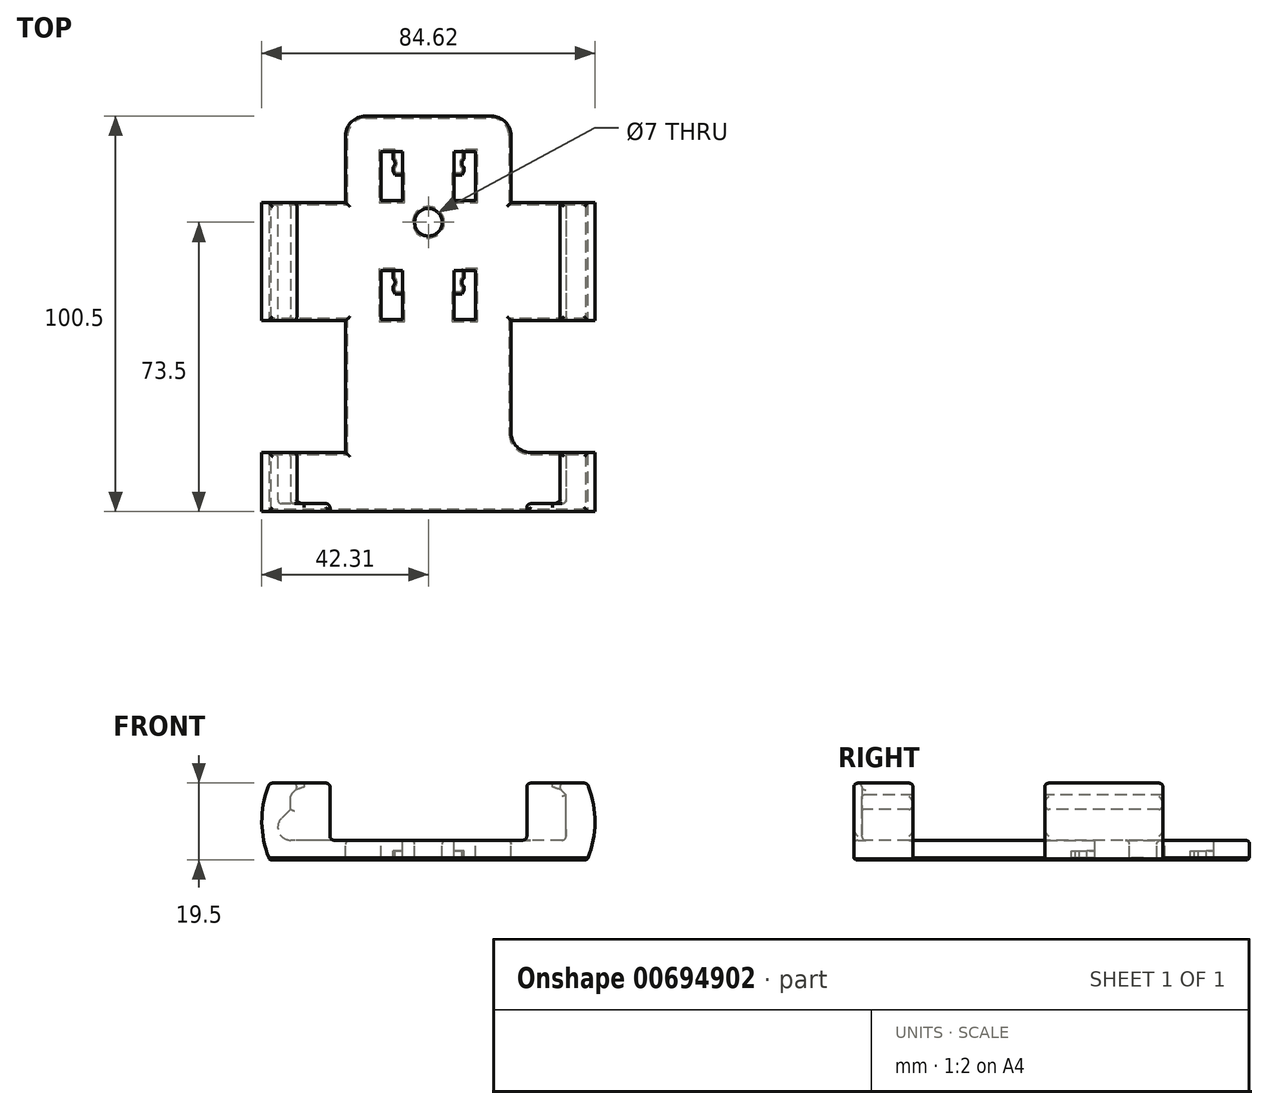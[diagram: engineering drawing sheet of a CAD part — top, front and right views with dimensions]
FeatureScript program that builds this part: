
annotation { "Feature Type Name" : "Feature", "Feature Type Description" : "" }
export const myFeature = defineFeature(function(context is Context, id is Id, definition is map)
    precondition{}
    {
        {
            var Q0;
            Q0=qCreatedBy(makeId("Top.planeOp"),FACE);
            var sketch = newSketch(context, id + "F0", { "sketchPlane" : qUnion([Q0])});
            skLineSegment(sketch, "E0.bottom", {"start": v(-35, 71.5) * mm, "end": v(35, 71.5) * mm});
            skLineSegment(sketch, "E0.top", {"start": v(-35, -71.5) * mm, "end": v(35, -71.5) * mm});
            skLineSegment(sketch, "E0.left", {"start": v(-35, 71.5) * mm, "end": v(-35, -71.5) * mm});
            skLineSegment(sketch, "E0.right", {"start": v(35, 71.5) * mm, "end": v(35, -71.5) * mm});
            skLineSegment(sketch, "E1", {"start": v(35, 71.5) * mm, "end": v(0, 0) * mm, "construction": true});
            skLineSegment(sketch, "E2.bottom", {"start": v(-55, 35.5) * mm, "end": v(55, 35.5) * mm});
            skLineSegment(sketch, "E2.top", {"start": v(-55, 16.5) * mm, "end": v(55, 16.5) * mm});
            skLineSegment(sketch, "E2.left", {"start": v(-55, 35.5) * mm, "end": v(-55, 16.5) * mm});
            skLineSegment(sketch, "E2.right", {"start": v(55, 35.5) * mm, "end": v(55, 16.5) * mm});
            skLineSegment(sketch, "E3.bottom", {"start": v(-35, 71.5) * mm, "end": v(-38.25, 71.5) * mm});
            skLineSegment(sketch, "E3.top", {"start": v(-35, -71.5) * mm, "end": v(-38.25, -71.5) * mm});
            skLineSegment(sketch, "E3.right", {"start": v(-38.25, 71.5) * mm, "end": v(-38.25, -71.5) * mm});
            skLineSegment(sketch, "E4", {"start": v(-35, 71.5) * mm, "end": v(0, 0) * mm, "construction": true});
            skLineSegment(sketch, "E5", {"start": v(0, 0) * mm, "end": v(-35, -71.5) * mm, "construction": true});
            skLineSegment(sketch, "E6", {"start": v(0, 0) * mm, "end": v(35, -71.5) * mm, "construction": true});
            skSolve(sketch);
        }
        {
            var Q0;
            Q0=qCreatedBy(makeId("Top.planeOp"),FACE);
            var sketch = newSketch(context, id + "F1", { "sketchPlane" : qUnion([Q0])});
            skLineSegment(sketch, "E7", {"start": v(-12, 5.5) * mm, "end": v(-6.5, 5.5) * mm});
            skLineSegment(sketch, "E8", {"start": v(-6.5, 5.5) * mm, "end": v(-6.5, 12) * mm});
            skLineSegment(sketch, "E9", {"start": v(-6.5, 12) * mm, "end": v(-8.5, 12) * mm});
            skLineSegment(sketch, "E10", {"start": v(-8.5, 12) * mm, "end": v(-9, 13) * mm});
            skLineSegment(sketch, "E11", {"start": v(-9, 13) * mm, "end": v(-9, 14) * mm});
            skLineSegment(sketch, "E12", {"start": v(-12, 5.5) * mm, "end": v(-12, 18) * mm});
            skLineSegment(sketch, "E13", {"start": v(-12, 18) * mm, "end": v(-9, 18) * mm});
            skLineSegment(sketch, "E14", {"start": v(-9, 18) * mm, "end": v(-9, 16) * mm});
            skLineSegment(sketch, "E15", {"start": v(-9, 16) * mm, "end": v(-9, 14) * mm, "construction": true});
            skLineSegment(sketch, "E16", {"start": v(-9, 15) * mm, "end": v(-8.5, 15) * mm, "construction": true});
            skArc(sketch, "E17", {"start": v(-9, 14) * mm, "mid": v(-8.5, 15) * mm, "end": v(-9, 16) * mm});
            skLineSegment(sketch, "E18", {"start": v(-9, 18) * mm, "end": v(-6.5, 18) * mm});
            skLineSegment(sketch, "E19", {"start": v(-6.5, 12) * mm, "end": v(-6.5, 18) * mm});
            skLineSegment(sketch, "E20", {"start": v(-12, -24.75) * mm, "end": v(-6.5, -24.75) * mm});
            skLineSegment(sketch, "E21", {"start": v(-6.5, -24.75) * mm, "end": v(-6.5, -18.25) * mm});
            skLineSegment(sketch, "E22", {"start": v(-6.5, -18.25) * mm, "end": v(-8.5, -18.25) * mm});
            skLineSegment(sketch, "E23", {"start": v(-8.5, -18.25) * mm, "end": v(-9, -17.25) * mm});
            skLineSegment(sketch, "E24", {"start": v(-9, -17.25) * mm, "end": v(-9, -16.25) * mm});
            skLineSegment(sketch, "E25", {"start": v(-12, -24.75) * mm, "end": v(-12, -12.25) * mm});
            skLineSegment(sketch, "E26", {"start": v(-12, -12.25) * mm, "end": v(-9, -12.25) * mm});
            skLineSegment(sketch, "E27", {"start": v(-9, -12.25) * mm, "end": v(-9, -14.25) * mm});
            skLineSegment(sketch, "E28", {"start": v(-9, -14.25) * mm, "end": v(-9, -16.25) * mm, "construction": true});
            skLineSegment(sketch, "E29", {"start": v(-9, -15.25) * mm, "end": v(-8.5, -15.25) * mm, "construction": true});
            skArc(sketch, "E30", {"start": v(-9, -16.25) * mm, "mid": v(-8.5, -15.25) * mm, "end": v(-9, -14.25) * mm});
            skLineSegment(sketch, "E31", {"start": v(-9, -12.25) * mm, "end": v(-6.5, -12.25) * mm});
            skLineSegment(sketch, "E32", {"start": v(-6.5, -18.25) * mm, "end": v(-6.5, -12.25) * mm});
            skLineSegment(sketch, "E33", {"start": v(-12, 18) * mm, "end": v(-15.54, 21.53) * mm, "construction": true});
            skLineSegment(sketch, "E34", {"start": v(-6.5, 18) * mm, "end": v(-7.92, 19.4) * mm, "construction": true});
            skLineSegment(sketch, "E35.MirrorCS", {"start": v(9, 15) * mm, "end": v(8.5, 15) * mm, "construction": true});
            skLineSegment(sketch, "E36.MirrorCS", {"start": v(9, 16) * mm, "end": v(9, 14) * mm, "construction": true});
            skLineSegment(sketch, "E37.MirrorCS", {"start": v(9, -14.25) * mm, "end": v(9, -16.25) * mm, "construction": true});
            skLineSegment(sketch, "E38.MirrorCS", {"start": v(9, 18) * mm, "end": v(9, 16) * mm});
            skArc(sketch, "E39.MirrorCS", {"start": v(9, 14) * mm, "mid": v(8.5, 15) * mm, "end": v(9, 16) * mm});
            skLineSegment(sketch, "E40.MirrorCS", {"start": v(8.5, -18.25) * mm, "end": v(9, -17.25) * mm});
            skArc(sketch, "E41.MirrorCS", {"start": v(9, -16.25) * mm, "mid": v(8.5, -15.25) * mm, "end": v(9, -14.25) * mm});
            skLineSegment(sketch, "E42.MirrorCS", {"start": v(8.5, 12) * mm, "end": v(9, 13) * mm});
            skLineSegment(sketch, "E43.MirrorCS", {"start": v(9, 13) * mm, "end": v(9, 14) * mm});
            skLineSegment(sketch, "E44.MirrorCS", {"start": v(9, -17.25) * mm, "end": v(9, -16.25) * mm});
            skLineSegment(sketch, "E45.MirrorCS", {"start": v(9, -15.25) * mm, "end": v(8.5, -15.25) * mm, "construction": true});
            skLineSegment(sketch, "E46.MirrorCS", {"start": v(9, -12.25) * mm, "end": v(9, -14.25) * mm});
            skLineSegment(sketch, "E47.MirrorCS", {"start": v(12, 18) * mm, "end": v(15.54, 21.53) * mm, "construction": true});
            skLineSegment(sketch, "E48.MirrorCS", {"start": v(6.5, 18) * mm, "end": v(7.92, 19.4) * mm, "construction": true});
            skLineSegment(sketch, "E49.MirrorCS", {"start": v(6.5, -18.25) * mm, "end": v(8.5, -18.25) * mm});
            skLineSegment(sketch, "E50.MirrorCS", {"start": v(6.5, 12) * mm, "end": v(8.5, 12) * mm});
            skLineSegment(sketch, "E51.MirrorCS", {"start": v(9, -12.25) * mm, "end": v(6.5, -12.25) * mm});
            skLineSegment(sketch, "E52.MirrorCS", {"start": v(12, 18) * mm, "end": v(9, 18) * mm});
            skLineSegment(sketch, "E53.MirrorCS", {"start": v(9, 18) * mm, "end": v(6.5, 18) * mm});
            skLineSegment(sketch, "E54.MirrorCS", {"start": v(12, -12.25) * mm, "end": v(9, -12.25) * mm});
            skLineSegment(sketch, "E55.MirrorCS", {"start": v(6.5, -18.25) * mm, "end": v(6.5, -12.25) * mm});
            skLineSegment(sketch, "E56.MirrorCS", {"start": v(6.5, 12) * mm, "end": v(6.5, 18) * mm});
            skLineSegment(sketch, "E57.MirrorCS", {"start": v(6.5, -24.75) * mm, "end": v(6.5, -18.25) * mm});
            skLineSegment(sketch, "E58.MirrorCS", {"start": v(12, 5.5) * mm, "end": v(6.5, 5.5) * mm});
            skLineSegment(sketch, "E59.MirrorCS", {"start": v(6.5, 5.5) * mm, "end": v(6.5, 12) * mm});
            skLineSegment(sketch, "E60.MirrorCS", {"start": v(12, -24.75) * mm, "end": v(6.5, -24.75) * mm});
            skLineSegment(sketch, "E61.MirrorCS", {"start": v(12, 5.5) * mm, "end": v(12, 18) * mm});
            skLineSegment(sketch, "E62.MirrorCS", {"start": v(12, -24.75) * mm, "end": v(12, -12.25) * mm});
            skSolve(sketch);
        }
        {
            var Q0;
            Q0=qCreatedBy(makeId("Top.planeOp"),FACE);
            var sketch = newSketch(context, id + "F2", { "sketchPlane" : qUnion([Q0])});
            skLineSegment(sketch, "E63.bottom", {"start": v(-21, 27) * mm, "end": v(21, 27) * mm});
            skLineSegment(sketch, "E63.top", {"start": v(-21, -27) * mm, "end": v(21, -27) * mm});
            skLineSegment(sketch, "E63.left", {"start": v(-21, 27) * mm, "end": v(-21, -27) * mm});
            skLineSegment(sketch, "E63.right", {"start": v(21, 27) * mm, "end": v(21, -27) * mm});
            skLineSegment(sketch, "E64", {"start": v(21, 27) * mm, "end": v(-21, -27) * mm, "construction": true});
            skLineSegment(sketch, "E65.top", {"start": v(-21, -71.5) * mm, "end": v(21, -71.5) * mm});
            skLineSegment(sketch, "E65.left", {"start": v(-21, -27) * mm, "end": v(-21, -71.5) * mm});
            skLineSegment(sketch, "E65.right", {"start": v(21, -27) * mm, "end": v(21, -71.5) * mm});
            skLineSegment(sketch, "E66.bottom", {"start": v(-21, 5) * mm, "end": v(-40.25, 5) * mm});
            skLineSegment(sketch, "E66.top", {"start": v(-21, -25) * mm, "end": v(-40.25, -25) * mm});
            skLineSegment(sketch, "E66.left", {"start": v(-21, 5) * mm, "end": v(-21, -25) * mm});
            skLineSegment(sketch, "E66.right", {"start": v(-40.25, 5) * mm, "end": v(-40.25, -25) * mm});
            skLineSegment(sketch, "E67.bottom", {"start": v(21, 5) * mm, "end": v(40.25, 5) * mm});
            skLineSegment(sketch, "E67.top", {"start": v(21, -25) * mm, "end": v(40.25, -25) * mm});
            skLineSegment(sketch, "E67.left", {"start": v(21, 5) * mm, "end": v(21, -25) * mm});
            skLineSegment(sketch, "E67.right", {"start": v(40.25, 5) * mm, "end": v(40.25, -25) * mm});
            skLineSegment(sketch, "E68.bottom", {"start": v(-40.25, -58.5) * mm, "end": v(40.25, -58.5) * mm});
            skLineSegment(sketch, "E68.top", {"start": v(-40.25, -73.5) * mm, "end": v(40.25, -73.5) * mm});
            skLineSegment(sketch, "E68.left", {"start": v(-40.25, -58.5) * mm, "end": v(-40.25, -73.5) * mm});
            skLineSegment(sketch, "E68.right", {"start": v(40.25, -58.5) * mm, "end": v(40.25, -73.5) * mm});
            skPoint(sketch, "E69", {"position": v(0, 20) * mm});
            skPoint(sketch, "E70", {"position": v(0, -20) * mm});
            skSolve(sketch);
        }
        {
            var Q0;
            Q0=qCreatedBy(makeId("Front.planeOp"),FACE);
            var Q1;
            Q1=sQuery(id+"F2.wireOp",VERTEX,"E65.top.start");
            cPlane(context, id + "F3", {"entities" : qUnion([Q0, Q1]), "cplaneType" : CPlaneType.PLANE_POINT, "offset" : 25 * mm, "width" : 150 * mm, "height" : 150 * mm});
        }
        {
            var Q0;
            Q0=qCreatedBy(id+"F3.planeOp",FACE);
            var sketch = newSketch(context, id + "F4", { "sketchPlane" : qUnion([Q0])});
            skLineSegment(sketch, "E71", {"start": v(35, 0) * mm, "end": v(-35, 0) * mm});
            skLineSegment(sketch, "E72", {"start": v(-32, 14.5) * mm, "end": v(-40.31, 14.5) * mm});
            skLineSegment(sketch, "E73", {"start": v(-40.31, -5) * mm, "end": v(40.31, -5) * mm});
            skLineSegment(sketch, "E74", {"start": v(40.31, 14.5) * mm, "end": v(32, 14.5) * mm});
            skLineSegment(sketch, "E75", {"start": v(32, 14.5) * mm, "end": v(32, 14.5) * mm});
            skArc(sketch, "E76", {"start": v(-40.31, 14.5) * mm, "mid": v(-42.31, 4.75) * mm, "end": v(-40.31, -5) * mm});
            skArc(sketch, "E77", {"start": v(40.31, -5) * mm, "mid": v(42.31, 4.75) * mm, "end": v(40.31, 14.5) * mm});
            skLineSegment(sketch, "E78", {"start": v(-32, 14.5) * mm, "end": v(-25, 14.5) * mm});
            skLineSegment(sketch, "E79", {"start": v(-25, 14.5) * mm, "end": v(-25, 0) * mm});
            skLineSegment(sketch, "E80", {"start": v(32, 14.5) * mm, "end": v(25, 14.5) * mm});
            skLineSegment(sketch, "E81", {"start": v(25, 14.5) * mm, "end": v(25, 0) * mm});
            skLineSegment(sketch, "E82", {"start": v(-32, 14.5) * mm, "end": v(-33.5, 13) * mm});
            skLineSegment(sketch, "E83", {"start": v(-33.5, 13) * mm, "end": v(-35, 11.5) * mm});
            skLineSegment(sketch, "E84", {"start": v(35, 0) * mm, "end": v(35, 6.5) * mm});
            skLineSegment(sketch, "E85", {"start": v(35, 6.5) * mm, "end": v(35, 11.5) * mm});
            skLineSegment(sketch, "E86", {"start": v(32, 14.5) * mm, "end": v(35, 11.5) * mm});
            skLineSegment(sketch, "E87", {"start": v(-40.31, 14.5) * mm, "end": v(-40.31, -5) * mm, "construction": true});
            skArc(sketch, "E88", {"start": v(-35, 0) * mm, "mid": v(-38, 2) * mm, "end": v(-37.3, 5.55) * mm});
            skLineSegment(sketch, "E89", {"start": v(-35, 7.85) * mm, "end": v(-37.3, 5.55) * mm});
            skLineSegment(sketch, "E90", {"start": v(-35, 7.85) * mm, "end": v(-35, 11.5) * mm});
            skLineSegment(sketch, "E91", {"start": v(-37.3, 5.55) * mm, "end": v(-37.3, 5.55) * mm});
            skArc(sketch, "E92", {"start": v(-37.3, 5.55) * mm, "mid": v(-36.24, 6.25) * mm, "end": v(-35, 6.5) * mm, "construction": true});
            skPoint(sketch, "E93.orphan", {"position": v(-49.26, 0) * mm});
            skSolve(sketch);
        }
        {
            var Q0;
            Q0=makeQuery(id+"F4.imprint","IMPRINT",FACE,{"disambiguationData":[TD([[makeQuery(id+"F4.imprint","IMPRINT",EDGE,{"derivedFrom":sQuery(id+"F4.wireOp",EDGE,"E72")}),1.0]])]});
            var Q1;
            Q1=sQuery(id+"F2.wireOp",VERTEX,"E68.bottom.start");
            extrude(context, id + "F5", {"entities" : qUnion([Q0]), "endBound" : BoundingType.UP_TO_VERTEX, "oppositeDirection" : true, "depth" : 25 * mm, "endBoundEntityVertex" : qUnion([Q1]), "offsetDistance" : 25 * mm});
        }
        {
            var Q0;
            Q0=makeQuery(id+"F4.imprint","IMPRINT",FACE,{"disambiguationData":[TD([[makeQuery(id+"F4.imprint","IMPRINT",EDGE,{"derivedFrom":sQuery(id+"F4.wireOp",EDGE,"E78")}),-1.0]])]});
            var Q1;
            Q1=makeQuery(id+"F4.imprint","IMPRINT",FACE,{"disambiguationData":[TD([[makeQuery(id+"F4.imprint","IMPRINT",EDGE,{"derivedFrom":sQuery(id+"F4.wireOp",EDGE,"E80")}),1.0]])]});
            var Q2;
            Q2=makeQuery(id+"F4.imprint","IMPRINT",FACE,{"disambiguationData":[TD([[makeQuery(id+"F4.imprint","IMPRINT",EDGE,{"derivedFrom":sQuery(id+"F4.wireOp",EDGE,"E72")}),1.0]])]});
            var Q3;
            Q3=sQuery(id+"F2.wireOp",VERTEX,"E68.left.end");
            extrude(context, id + "F6", {"entities" : qUnion([Q0, Q1, Q2]), "operationType" : NewBodyOperationType.ADD, "endBound" : BoundingType.UP_TO_VERTEX, "depth" : 25 * mm, "endBoundEntityVertex" : qUnion([Q3]), "offsetDistance" : 25 * mm});
        }
        {
            var Q0;
            Q0=makeQuery(id+"F4.imprint","IMPRINT",FACE,{"disambiguationData":[TD([[makeQuery(id+"F4.imprint","IMPRINT",EDGE,{"derivedFrom":sQuery(id+"F4.wireOp",EDGE,"E72")}),1.0]])]});
            var Q1;
            Q1=sQuery(id+"F2.wireOp",VERTEX,"E67.bottom.end");
            var Q2;
            Q2=sQuery(id+"F2.wireOp",VERTEX,"E67.right.end");
            extrude(context, id + "F7", {"entities" : qUnion([Q0]), "endBound" : BoundingType.UP_TO_VERTEX, "oppositeDirection" : true, "depth" : 25 * mm, "endBoundEntityVertex" : qUnion([Q1]), "offsetDistance" : 25 * mm, "hasSecondDirection" : true, "secondDirectionBound" : SecondDirectionBoundingType.UP_TO_VERTEX, "secondDirectionOppositeDirection" : true, "secondDirectionDepth" : 25 * mm, "secondDirectionBoundEntityVertex" : qUnion([Q2])});
        }
        {
            var Q0;
            {var subQ1=sQuery(id+"F2.wireOp",EDGE,"E63.bottom");Q0=makeQuery(id+"F2.imprint","IMPRINT",FACE,{"disambiguationData":[TD([[makeQuery(id+"F2.imprint","IMPRINT",EDGE,{"derivedFrom":subQ1}),-1.0]])]});}
            var Q1;
            {var subQ0=sQuery(id+"F2.wireOp",EDGE,"E63.top");Q1=makeQuery(id+"F2.imprint","IMPRINT",FACE,{"disambiguationData":[TD([[makeQuery(id+"F2.imprint","IMPRINT",EDGE,{"derivedFrom":subQ0}),-1.0]])]});}
            var Q2;
            Q2=makeQuery(id+"F6.opExtrude","CAP_VERTEX",VERTEX,{"disambiguationData":[OSD([sQuery(id+"F4.wireOp",EDGE,"E73"),sQuery(id+"F4.wireOp",EDGE,"E76"),dummyQuery(id+"F6.vertexPlane.planeOp",FACE)])],"isStart":false});
            extrude(context, id + "F8", {"entities" : qUnion([Q0, Q1]), "endBound" : BoundingType.UP_TO_VERTEX, "oppositeDirection" : true, "depth" : 25 * mm, "endBoundEntityVertex" : qUnion([Q2]), "offsetDistance" : 25 * mm});
        }
        {
            var Q0;
            Q0=makeQuery(id+"F5.opExtrude","SWEPT_BODY",BODY,{"disambiguationData":[OSD([sQuery(id+"F4.wireOp",EDGE,"E71"),sQuery(id+"F4.wireOp",EDGE,"sbdDi5I9-Yebq-qmN7-GLHp-3G1XwB9cKRCZ"),sQuery(id+"F4.wireOp",EDGE,"7URjV5Ms-kFcT-YtzM-ZppO-VChNSRZk8awo"),sQuery(id+"F4.wireOp",EDGE,"zq0j43Qj-IFnj-aGb7-oLl1-zX5iOFrslPZI"),sQuery(id+"F4.wireOp",EDGE,"k48rp8DH-MXxx-a3kQ-F4OR-XtvpYe2jZDF6"),sQuery(id+"F4.wireOp",EDGE,"ZQmb1dzz-Gxe3-Qxpy-tlJK-SNzGoLeYOMF0"),sQuery(id+"F4.wireOp",EDGE,"E72"),sQuery(id+"F4.wireOp",EDGE,"E73"),sQuery(id+"F4.wireOp",EDGE,"E74"),sQuery(id+"F4.wireOp",EDGE,"E75"),sQuery(id+"F4.wireOp",EDGE,"qAfCrrqd-AJ75-G8RO-JwNo-VFnenWKlcyLA"),sQuery(id+"F4.wireOp",EDGE,"rlMWnyCU-j4gb-ryVS-FNKK-qwGZLt9JwQKd"),sQuery(id+"F4.wireOp",EDGE,"E76"),sQuery(id+"F4.wireOp",EDGE,"E77")])]});
            var Q1;
            Q1=makeQuery(id+"F7.opExtrude","SWEPT_BODY",BODY,{"disambiguationData":[OSD([sQuery(id+"F4.wireOp",EDGE,"E71"),sQuery(id+"F4.wireOp",EDGE,"sbdDi5I9-Yebq-qmN7-GLHp-3G1XwB9cKRCZ"),sQuery(id+"F4.wireOp",EDGE,"7URjV5Ms-kFcT-YtzM-ZppO-VChNSRZk8awo"),sQuery(id+"F4.wireOp",EDGE,"zq0j43Qj-IFnj-aGb7-oLl1-zX5iOFrslPZI"),sQuery(id+"F4.wireOp",EDGE,"k48rp8DH-MXxx-a3kQ-F4OR-XtvpYe2jZDF6"),sQuery(id+"F4.wireOp",EDGE,"ZQmb1dzz-Gxe3-Qxpy-tlJK-SNzGoLeYOMF0"),sQuery(id+"F4.wireOp",EDGE,"E72"),sQuery(id+"F4.wireOp",EDGE,"E73"),sQuery(id+"F4.wireOp",EDGE,"E74"),sQuery(id+"F4.wireOp",EDGE,"E75"),sQuery(id+"F4.wireOp",EDGE,"qAfCrrqd-AJ75-G8RO-JwNo-VFnenWKlcyLA"),sQuery(id+"F4.wireOp",EDGE,"rlMWnyCU-j4gb-ryVS-FNKK-qwGZLt9JwQKd"),sQuery(id+"F4.wireOp",EDGE,"E76"),sQuery(id+"F4.wireOp",EDGE,"E77")])]});
            var Q2;
            Q2=makeQuery(id+"F8.opExtrude","SWEPT_BODY",BODY,{"disambiguationData":[OSD([sQuery(id+"F2.wireOp",EDGE,"E63.bottom"),sQuery(id+"F2.wireOp",EDGE,"E63.left"),sQuery(id+"F2.wireOp",EDGE,"E63.right"),sQuery(id+"F2.wireOp",EDGE,"E65.left"),sQuery(id+"F2.wireOp",EDGE,"E65.right"),sQuery(id+"F2.wireOp",EDGE,"E66.left"),sQuery(id+"F2.wireOp",EDGE,"E67.left"),sQuery(id+"F2.wireOp",EDGE,"E68.bottom")])]});
            booleanBodies(context, id + "F9", {"operationType" : BooleanOperationType.UNION, "tools" : qUnion([Q0, Q1, Q2])});
        }
        {
            var Q0;
            Q0=sQuery(id+"F0.wireOp",VERTEX,"E1.end");
            var Q1;
            Q1=makeQuery(id+"F5.opExtrude","SWEPT_BODY",BODY,{"disambiguationData":[OSD([sQuery(id+"F4.wireOp",EDGE,"E71"),sQuery(id+"F4.wireOp",EDGE,"sbdDi5I9-Yebq-qmN7-GLHp-3G1XwB9cKRCZ"),sQuery(id+"F4.wireOp",EDGE,"7URjV5Ms-kFcT-YtzM-ZppO-VChNSRZk8awo"),sQuery(id+"F4.wireOp",EDGE,"zq0j43Qj-IFnj-aGb7-oLl1-zX5iOFrslPZI"),sQuery(id+"F4.wireOp",EDGE,"k48rp8DH-MXxx-a3kQ-F4OR-XtvpYe2jZDF6"),sQuery(id+"F4.wireOp",EDGE,"ZQmb1dzz-Gxe3-Qxpy-tlJK-SNzGoLeYOMF0"),sQuery(id+"F4.wireOp",EDGE,"E72"),sQuery(id+"F4.wireOp",EDGE,"E73"),sQuery(id+"F4.wireOp",EDGE,"E74"),sQuery(id+"F4.wireOp",EDGE,"E75"),sQuery(id+"F4.wireOp",EDGE,"qAfCrrqd-AJ75-G8RO-JwNo-VFnenWKlcyLA"),sQuery(id+"F4.wireOp",EDGE,"rlMWnyCU-j4gb-ryVS-FNKK-qwGZLt9JwQKd"),sQuery(id+"F4.wireOp",EDGE,"E76"),sQuery(id+"F4.wireOp",EDGE,"E77")])]});
            hole(context, id + "F10", {"style" : HoleStyle.SIMPLE, "endStyle" : HoleEndStyle.THROUGH, "holeDiameter" : 7 * mm, "majorDiameter" : 5 * mm, "isTappedThrough" : true, "tappedDepth" : 12 * mm, "tapClearance" : 3, "locations" : qUnion([Q0]), "scope" : qUnion([Q1])});
        }
        {
            var Q0;
            Q0=makeQuery(id+"F8.opExtrude","SWEPT_EDGE",EDGE,{"disambiguationData":[OSD([sQuery(id+"F2.wireOp",EDGE,"E63.bottom"),sQuery(id+"F2.wireOp",EDGE,"E63.left")])]});
            var Q1;
            Q1=makeQuery(id+"F8.opExtrude","SWEPT_EDGE",EDGE,{"disambiguationData":[OSD([sQuery(id+"F2.wireOp",EDGE,"E63.bottom"),sQuery(id+"F2.wireOp",EDGE,"E63.right")])]});
            var Q2;
            Q2=makeQuery(id+"F9.opBoolean","INTERSECT",EDGE,{"derivedFrom":[makeQuery(id+"F7.opExtrude","CAP_FACE",FACE,{"disambiguationData":[OSD([dummyQuery(id+"F7.vertexPlane.planeOp",FACE)])],"isStart":false}),makeQuery(id+"F8.opExtrude","SWEPT_FACE",FACE,{"disambiguationData":[OSD([sQuery(id+"F2.wireOp",EDGE,"E63.left"),sQuery(id+"F2.wireOp",EDGE,"E65.left"),sQuery(id+"F2.wireOp",EDGE,"E66.left")])]})]});
            var Q3;
            Q3=makeQuery(id+"F8.opExtrude","SWEPT_EDGE",EDGE,{"disambiguationData":[OSD([sQuery(id+"F2.wireOp",EDGE,"E65.left"),sQuery(id+"F2.wireOp",EDGE,"E68.bottom")])]});
            var Q4;
            Q4=makeQuery(id+"F9.opBoolean","INTERSECT",EDGE,{"derivedFrom":[makeQuery(id+"F7.opExtrude","CAP_FACE",FACE,{"disambiguationData":[OSD([dummyQuery(id+"F7.vertexPlane.planeOp",FACE)])],"isStart":false}),makeQuery(id+"F8.opExtrude","SWEPT_FACE",FACE,{"disambiguationData":[OSD([sQuery(id+"F2.wireOp",EDGE,"E63.right"),sQuery(id+"F2.wireOp",EDGE,"E65.right"),sQuery(id+"F2.wireOp",EDGE,"E67.left")])]})]});
            var Q5;
            Q5=makeQuery(id+"F8.opExtrude","SWEPT_EDGE",EDGE,{"disambiguationData":[OSD([sQuery(id+"F2.wireOp",EDGE,"E65.right"),sQuery(id+"F2.wireOp",EDGE,"E68.bottom")])]});
            var Q6;
            Q6=makeQuery(id+"F9.opBoolean","INTERSECT",EDGE,{"derivedFrom":[makeQuery(id+"F7.opExtrude","CAP_FACE",FACE,{"disambiguationData":[OSD([dummyQuery(id+"F7.secondVertexPlane.planeOp",FACE)])],"isStart":true}),makeQuery(id+"F8.opExtrude","SWEPT_FACE",FACE,{"disambiguationData":[OSD([sQuery(id+"F2.wireOp",EDGE,"E63.left"),sQuery(id+"F2.wireOp",EDGE,"E65.left"),sQuery(id+"F2.wireOp",EDGE,"E66.left")])]})]});
            var Q7;
            Q7=makeQuery(id+"F9.opBoolean","INTERSECT",EDGE,{"derivedFrom":[makeQuery(id+"F7.opExtrude","CAP_FACE",FACE,{"disambiguationData":[OSD([dummyQuery(id+"F7.secondVertexPlane.planeOp",FACE)])],"isStart":true}),makeQuery(id+"F8.opExtrude","SWEPT_FACE",FACE,{"disambiguationData":[OSD([sQuery(id+"F2.wireOp",EDGE,"E63.right"),sQuery(id+"F2.wireOp",EDGE,"E65.right"),sQuery(id+"F2.wireOp",EDGE,"E67.left")])]})]});
            fillet(context, id + "F11", {"entities" : qUnion([Q0, Q1, Q2, Q3, Q4, Q5, Q6, Q7]), "radius" : 5 * mm, "tangentPropagation" : true, "allowEdgeOverflow" : false});
        }
        {
            var Q0;
            {var subQ0=sQuery(id+"F4.wireOp",EDGE,"E71");Q0=makeQuery(id+"F9.opBoolean","MERGE",FACE,{"derivedFrom":[makeQuery(id+"F6.boolean.opBoolean","MERGE",FACE,{"derivedFrom":[makeQuery(id+"F5.opExtrude","SWEPT_FACE",FACE,{"disambiguationData":[OSD([subQ0])]}),makeQuery(id+"F6.opExtrude","SWEPT_FACE",FACE,{"disambiguationData":[OSD([subQ0])]})]}),makeQuery(id+"F7.opExtrude","SWEPT_FACE",FACE,{"disambiguationData":[OSD([subQ0])]}),makeQuery(id+"F8.opExtrude","CAP_FACE",FACE,{"disambiguationData":[OSD([sQuery(id+"F2.wireOp",EDGE,"E63.bottom"),sQuery(id+"F2.wireOp",EDGE,"E63.left"),sQuery(id+"F2.wireOp",EDGE,"E63.right"),sQuery(id+"F2.wireOp",EDGE,"E65.left"),sQuery(id+"F2.wireOp",EDGE,"E65.right"),sQuery(id+"F2.wireOp",EDGE,"E66.left"),sQuery(id+"F2.wireOp",EDGE,"E67.left"),sQuery(id+"F2.wireOp",EDGE,"E68.bottom")])],"isStart":true})]});}
            var Q1;
            Q1=makeQuery(id+"F7.opExtrude","SWEPT_FACE",FACE,{"disambiguationData":[OSD([sQuery(id+"F4.wireOp",EDGE,"LpgQ50cI-rkaD-dWZC-SDoM-5TgKdtqdCB1Y"),sQuery(id+"F4.wireOp",EDGE,"8b8aca45-342e-4dc1-8e70-ffe43229b5f0")])]});
            var Q2;
            Q2=makeQuery(id+"F7.opExtrude","SWEPT_FACE",FACE,{"disambiguationData":[OSD([sQuery(id+"F4.wireOp",EDGE,"E74")])]});
            var Q3;
            Q3=makeQuery(id+"F7.opExtrude","TWEAK_EDGE",EDGE,{"derivedFrom":[makeQuery(id+"F4.imprint","IMPRINT",EDGE,{"derivedFrom":sQuery(id+"F4.wireOp",EDGE,"E77")}),dummyQuery(id+"F7.vertexPlane.planeOp",FACE)]});
            var Q4;
            Q4=makeQuery(id+"F7.opExtrude","TWEAK_EDGE",EDGE,{"derivedFrom":[makeQuery(id+"F4.imprint","IMPRINT",EDGE,{"derivedFrom":sQuery(id+"F4.wireOp",EDGE,"E77")}),dummyQuery(id+"F7.secondVertexPlane.planeOp",FACE)]});
            var Q5;
            Q5=makeQuery(id+"F7.opExtrude","SWEPT_FACE",FACE,{"disambiguationData":[OSD([sQuery(id+"F4.wireOp",EDGE,"4QVrSNSO-dE2i-KCaz-ZRgr-ALMQ5YD6hFyM")])]});
            var Q6;
            Q6=makeQuery(id+"F7.opExtrude","SWEPT_FACE",FACE,{"disambiguationData":[OSD([sQuery(id+"F4.wireOp",EDGE,"E82")])]});
            var Q7;
            Q7=makeQuery(id+"F7.opExtrude","SWEPT_FACE",FACE,{"disambiguationData":[OSD([sQuery(id+"F4.wireOp",EDGE,"E72")])]});
            var Q8;
            Q8=makeQuery(id+"F7.opExtrude","TWEAK_EDGE",EDGE,{"derivedFrom":[makeQuery(id+"F4.imprint","IMPRINT",EDGE,{"derivedFrom":sQuery(id+"F4.wireOp",EDGE,"E76")}),dummyQuery(id+"F7.vertexPlane.planeOp",FACE)]});
            var Q9;
            Q9=makeQuery(id+"F7.opExtrude","TWEAK_EDGE",EDGE,{"derivedFrom":[makeQuery(id+"F4.imprint","IMPRINT",EDGE,{"derivedFrom":sQuery(id+"F4.wireOp",EDGE,"E76")}),dummyQuery(id+"F7.secondVertexPlane.planeOp",FACE)]});
            var Q10;
            Q10=makeQuery(id+"F5.opExtrude","SWEPT_FACE",FACE,{"disambiguationData":[OSD([sQuery(id+"F4.wireOp",EDGE,"LpgQ50cI-rkaD-dWZC-SDoM-5TgKdtqdCB1Y"),sQuery(id+"F4.wireOp",EDGE,"8b8aca45-342e-4dc1-8e70-ffe43229b5f0")])]});
            var Q11;
            Q11=makeQuery(id+"F5.opExtrude","SWEPT_FACE",FACE,{"disambiguationData":[OSD([sQuery(id+"F4.wireOp",EDGE,"4QVrSNSO-dE2i-KCaz-ZRgr-ALMQ5YD6hFyM")])]});
            var Q12;
            Q12=makeQuery(id+"F5.opExtrude","SWEPT_FACE",FACE,{"disambiguationData":[OSD([sQuery(id+"F4.wireOp",EDGE,"E82")])]});
            var Q13;
            {var subQ0=sQuery(id+"F4.wireOp",EDGE,"E72");Q13=makeQuery(id+"F6.boolean.opBoolean","MERGE",FACE,{"derivedFrom":[makeQuery(id+"F5.opExtrude","SWEPT_FACE",FACE,{"disambiguationData":[OSD([subQ0])]}),makeQuery(id+"F6.opExtrude","SWEPT_FACE",FACE,{"disambiguationData":[OSD([subQ0,sQuery(id+"F4.wireOp",EDGE,"E78")])]})]});}
            var Q14;
            Q14=makeQuery(id+"F5.opExtrude","TWEAK_EDGE",EDGE,{"derivedFrom":[makeQuery(id+"F4.imprint","IMPRINT",EDGE,{"derivedFrom":sQuery(id+"F4.wireOp",EDGE,"E76")}),dummyQuery(id+"F5.vertexPlane.planeOp",FACE)]});
            var Q15;
            Q15=makeQuery(id+"F6.opExtrude","TWEAK_EDGE",EDGE,{"derivedFrom":[makeQuery(id+"F4.imprint","IMPRINT",EDGE,{"derivedFrom":sQuery(id+"F4.wireOp",EDGE,"E76")}),dummyQuery(id+"F6.vertexPlane.planeOp",FACE)]});
            var Q16;
            {var subQ0=sQuery(id+"F4.wireOp",EDGE,"E74");Q16=makeQuery(id+"F6.boolean.opBoolean","MERGE",FACE,{"derivedFrom":[makeQuery(id+"F5.opExtrude","SWEPT_FACE",FACE,{"disambiguationData":[OSD([subQ0])]}),makeQuery(id+"F6.opExtrude","SWEPT_FACE",FACE,{"disambiguationData":[OSD([subQ0])]})]});}
            var Q17;
            Q17=makeQuery(id+"F5.opExtrude","TWEAK_EDGE",EDGE,{"derivedFrom":[makeQuery(id+"F4.imprint","IMPRINT",EDGE,{"derivedFrom":sQuery(id+"F4.wireOp",EDGE,"E77")}),dummyQuery(id+"F5.vertexPlane.planeOp",FACE)]});
            var Q18;
            Q18=makeQuery(id+"F6.opExtrude","TWEAK_EDGE",EDGE,{"derivedFrom":[makeQuery(id+"F4.imprint","IMPRINT",EDGE,{"derivedFrom":sQuery(id+"F4.wireOp",EDGE,"E77")}),dummyQuery(id+"F6.vertexPlane.planeOp",FACE)]});
            var Q19;
            Q19=makeQuery(id+"F6.opExtrude","CAP_FACE",FACE,{"disambiguationData":[OSD([sQuery(id+"F4.wireOp",EDGE,"E71"),sQuery(id+"F4.wireOp",EDGE,"E72"),sQuery(id+"F4.wireOp",EDGE,"E73"),sQuery(id+"F4.wireOp",EDGE,"E74"),sQuery(id+"F4.wireOp",EDGE,"rlMWnyCU-j4gb-ryVS-FNKK-qwGZLt9JwQKd"),sQuery(id+"F4.wireOp",EDGE,"E76"),sQuery(id+"F4.wireOp",EDGE,"E77"),sQuery(id+"F4.wireOp",EDGE,"E78"),sQuery(id+"F4.wireOp",EDGE,"E79"),sQuery(id+"F4.wireOp",EDGE,"LpgQ50cI-rkaD-dWZC-SDoM-5TgKdtqdCB1Y"),sQuery(id+"F4.wireOp",EDGE,"8b8aca45-342e-4dc1-8e70-ffe43229b5f0")])],"isStart":true});
            fillet(context, id + "F12", {"entities" : qUnion([Q0, Q1, Q2, Q3, Q4, Q5, Q6, Q7, Q8, Q9, Q10, Q11, Q12, Q13, Q14, Q15, Q16, Q17, Q18, Q19]), "radius" : 1 * mm, "tangentPropagation" : true, "allowEdgeOverflow" : false});
        }
        {
            var Q0;
            Q0=makeQuery(id+"F1.imprint","IMPRINT",FACE,{"disambiguationData":[TD([[makeQuery(id+"F1.imprint","IMPRINT",EDGE,{"derivedFrom":sQuery(id+"F1.wireOp",EDGE,"E38.MirrorCS")}),1.0]])]});
            var Q1;
            Q1=makeQuery(id+"F1.imprint","IMPRINT",FACE,{"disambiguationData":[TD([[makeQuery(id+"F1.imprint","IMPRINT",EDGE,{"derivedFrom":sQuery(id+"F1.wireOp",EDGE,"E7")}),1.0]])]});
            var Q2;
            Q2=makeQuery(id+"F1.imprint","IMPRINT",FACE,{"disambiguationData":[TD([[makeQuery(id+"F1.imprint","IMPRINT",EDGE,{"derivedFrom":sQuery(id+"F1.wireOp",EDGE,"E40.MirrorCS")}),-1.0]])]});
            var Q3;
            Q3=makeQuery(id+"F1.imprint","IMPRINT",FACE,{"disambiguationData":[TD([[makeQuery(id+"F1.imprint","IMPRINT",EDGE,{"derivedFrom":sQuery(id+"F1.wireOp",EDGE,"E20")}),1.0]])]});
            var Q4;
            Q4=makeQuery(id+"F1.imprint","IMPRINT",FACE,{"disambiguationData":[TD([[makeQuery(id+"F1.imprint","IMPRINT",EDGE,{"derivedFrom":sQuery(id+"F1.wireOp",EDGE,"E9")}),-1.0]])]});
            var Q5;
            Q5=makeQuery(id+"F1.imprint","IMPRINT",FACE,{"disambiguationData":[TD([[makeQuery(id+"F1.imprint","IMPRINT",EDGE,{"derivedFrom":sQuery(id+"F1.wireOp",EDGE,"E38.MirrorCS")}),-1.0]])]});
            var Q6;
            Q6=makeQuery(id+"F1.imprint","IMPRINT",FACE,{"disambiguationData":[TD([[makeQuery(id+"F1.imprint","IMPRINT",EDGE,{"derivedFrom":sQuery(id+"F1.wireOp",EDGE,"E40.MirrorCS")}),1.0]])]});
            var Q7;
            Q7=makeQuery(id+"F1.imprint","IMPRINT",FACE,{"disambiguationData":[TD([[makeQuery(id+"F1.imprint","IMPRINT",EDGE,{"derivedFrom":sQuery(id+"F1.wireOp",EDGE,"E22")}),-1.0]])]});
            extrude(context, id + "F13", {"entities" : qUnion([Q0, Q1, Q2, Q3, Q4, Q5, Q6, Q7]), "operationType" : NewBodyOperationType.REMOVE, "oppositeDirection" : true, "depth" : 5 * mm, "offsetDistance" : 25 * mm});
        }
        {
            var Q0;
            Q0=makeQuery(id+"F1.imprint","IMPRINT",FACE,{"disambiguationData":[TD([[makeQuery(id+"F1.imprint","IMPRINT",EDGE,{"derivedFrom":sQuery(id+"F1.wireOp",EDGE,"E38.MirrorCS")}),-1.0]])]});
            var Q1;
            Q1=makeQuery(id+"F1.imprint","IMPRINT",FACE,{"disambiguationData":[TD([[makeQuery(id+"F1.imprint","IMPRINT",EDGE,{"derivedFrom":sQuery(id+"F1.wireOp",EDGE,"E9")}),-1.0]])]});
            var Q2;
            Q2=makeQuery(id+"F1.imprint","IMPRINT",FACE,{"disambiguationData":[TD([[makeQuery(id+"F1.imprint","IMPRINT",EDGE,{"derivedFrom":sQuery(id+"F1.wireOp",EDGE,"E40.MirrorCS")}),1.0]])]});
            var Q3;
            Q3=makeQuery(id+"F1.imprint","IMPRINT",FACE,{"disambiguationData":[TD([[makeQuery(id+"F1.imprint","IMPRINT",EDGE,{"derivedFrom":sQuery(id+"F1.wireOp",EDGE,"E22")}),-1.0]])]});
            extrude(context, id + "F14", {"entities" : qUnion([Q0, Q1, Q2, Q3]), "operationType" : NewBodyOperationType.ADD, "oppositeDirection" : true, "depth" : 5 * mm, "offsetDistance" : 25 * mm, "hasSecondDirection" : true, "secondDirectionOppositeDirection" : true, "secondDirectionDepth" : 2.75 * mm});
        }
        {
            var Q0;
            {var subQ0=sQuery(id+"F4.wireOp",EDGE,"E73");Q0=makeQuery(id+"F14.boolean.opBoolean","MERGE",FACE,{"derivedFrom":[makeQuery(id+"F9.opBoolean","MERGE",FACE,{"derivedFrom":[makeQuery(id+"F6.boolean.opBoolean","MERGE",FACE,{"derivedFrom":[makeQuery(id+"F5.opExtrude","SWEPT_FACE",FACE,{"disambiguationData":[OSD([subQ0])]}),makeQuery(id+"F6.opExtrude","SWEPT_FACE",FACE,{"disambiguationData":[OSD([subQ0])]})]}),makeQuery(id+"F7.opExtrude","SWEPT_FACE",FACE,{"disambiguationData":[OSD([subQ0])]}),makeQuery(id+"F8.opExtrude","CAP_FACE",FACE,{"disambiguationData":[OSD([dummyQuery(id+"F8.vertexPlane.planeOp",FACE)])],"isStart":false})]}),makeQuery(id+"F14.opExtrude","CAP_FACE",FACE,{"disambiguationData":[OSD([sQuery(id+"F1.wireOp",EDGE,"E9"),sQuery(id+"F1.wireOp",EDGE,"E10"),sQuery(id+"F1.wireOp",EDGE,"E11"),sQuery(id+"F1.wireOp",EDGE,"E14"),sQuery(id+"F1.wireOp",EDGE,"E17"),sQuery(id+"F1.wireOp",EDGE,"E18"),sQuery(id+"F1.wireOp",EDGE,"E19")])],"isStart":false}),makeQuery(id+"F14.opExtrude","CAP_FACE",FACE,{"disambiguationData":[OSD([sQuery(id+"F1.wireOp",EDGE,"E22"),sQuery(id+"F1.wireOp",EDGE,"E23"),sQuery(id+"F1.wireOp",EDGE,"E24"),sQuery(id+"F1.wireOp",EDGE,"E27"),sQuery(id+"F1.wireOp",EDGE,"E30"),sQuery(id+"F1.wireOp",EDGE,"E31"),sQuery(id+"F1.wireOp",EDGE,"E32")])],"isStart":false}),makeQuery(id+"F14.opExtrude","CAP_FACE",FACE,{"disambiguationData":[OSD([sQuery(id+"F1.wireOp",EDGE,"E38.MirrorCS"),sQuery(id+"F1.wireOp",EDGE,"E39.MirrorCS"),sQuery(id+"F1.wireOp",EDGE,"E42.MirrorCS"),sQuery(id+"F1.wireOp",EDGE,"E43.MirrorCS"),sQuery(id+"F1.wireOp",EDGE,"E50.MirrorCS"),sQuery(id+"F1.wireOp",EDGE,"E53.MirrorCS"),sQuery(id+"F1.wireOp",EDGE,"E56.MirrorCS")])],"isStart":false}),makeQuery(id+"F14.opExtrude","CAP_FACE",FACE,{"disambiguationData":[OSD([sQuery(id+"F1.wireOp",EDGE,"E40.MirrorCS"),sQuery(id+"F1.wireOp",EDGE,"E41.MirrorCS"),sQuery(id+"F1.wireOp",EDGE,"E44.MirrorCS"),sQuery(id+"F1.wireOp",EDGE,"E46.MirrorCS"),sQuery(id+"F1.wireOp",EDGE,"E49.MirrorCS"),sQuery(id+"F1.wireOp",EDGE,"E51.MirrorCS"),sQuery(id+"F1.wireOp",EDGE,"E55.MirrorCS")])],"isStart":false})]});}
            chamfer(context, id + "F15", {"entities" : qUnion([Q0]), "width" : .5 * mm, "tangentPropagation" : true});
        }
    });
